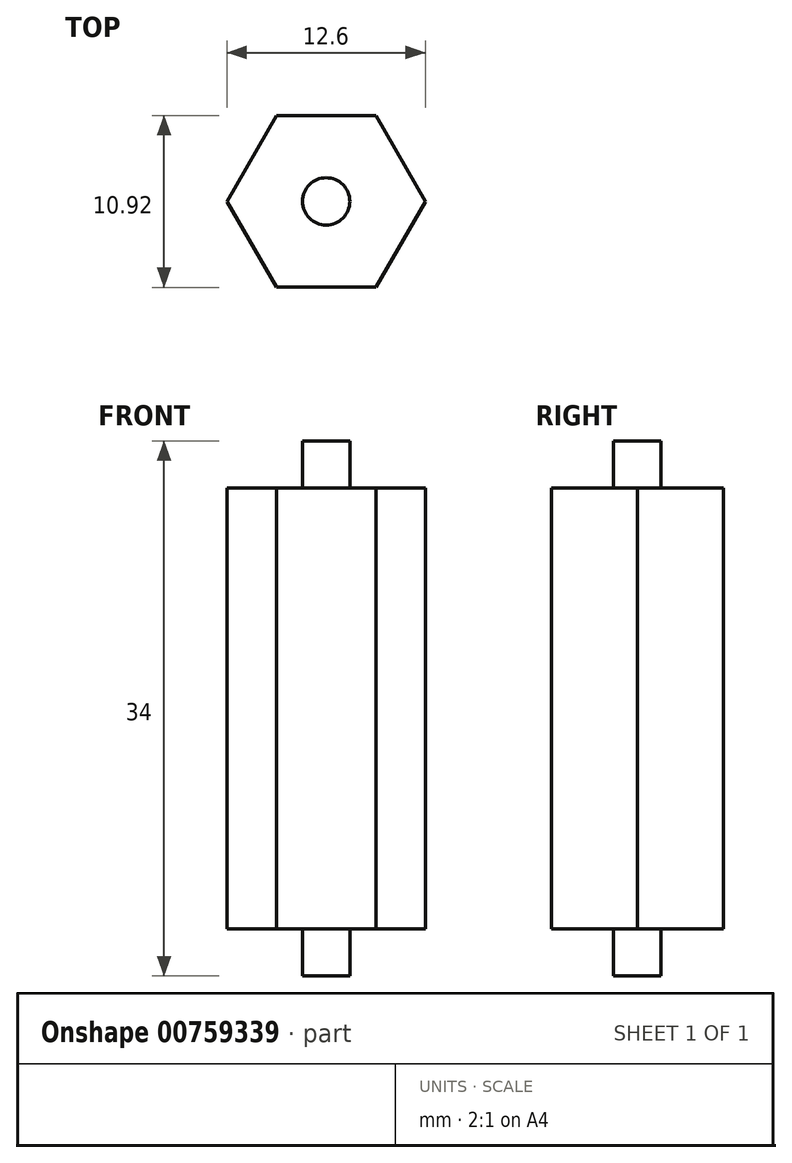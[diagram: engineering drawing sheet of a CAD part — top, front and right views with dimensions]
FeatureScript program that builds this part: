
annotation { "Feature Type Name" : "Feature", "Feature Type Description" : "" }
export const myFeature = defineFeature(function(context is Context, id is Id, definition is map)
    precondition{}
    {
        {
            var Q0;
            Q0=qCreatedBy(makeId("Top.planeOp"),FACE);
            var sketch = newSketch(context, id + "F0", { "sketchPlane" : qUnion([Q0])});
            skCircle(sketch, "E0.cCircle", {"center": v(0, 0) * mm, "radius": 5.46 * mm, "construction": true});
            skLineSegment(sketch, "E0.0", {"start": v(-3.15, 5.46) * mm, "end": v(3.15, 5.46) * mm});
            skLineSegment(sketch, "E0.1", {"start": v(3.15, 5.46) * mm, "end": v(6.3, 0) * mm});
            skLineSegment(sketch, "E0.2", {"start": v(6.3, 0) * mm, "end": v(3.15, -5.46) * mm});
            skLineSegment(sketch, "E0.3", {"start": v(3.15, -5.46) * mm, "end": v(-3.15, -5.46) * mm});
            skLineSegment(sketch, "E0.4", {"start": v(-3.15, -5.46) * mm, "end": v(-6.3, 0) * mm});
            skLineSegment(sketch, "E0.5", {"start": v(-6.3, 0) * mm, "end": v(-3.15, 5.46) * mm});
            skPoint(sketch, "E0.0.midPoint", {"position": v(0, 5.46) * mm});
            skSolve(sketch);
        }
        {
            var Q0;
            Q0=makeQuery(id+"F0.imprint","IMPRINT",FACE,{"disambiguationData":[TD([[makeQuery(id+"F0.imprint","IMPRINT",EDGE,{"derivedFrom":sQuery(id+"F0.wireOp",EDGE,"E0.0")}),-1.0]])]});
            extrude(context, id + "F1", {"entities" : qUnion([Q0]), "depth" : 28 * mm, "offsetDistance" : 25 * mm});
        }
        {
            var Q0;
            Q0=makeQuery(id+"F1.opExtrude","CAP_FACE",FACE,{"disambiguationData":[OSD([sQuery(id+"F0.wireOp",EDGE,"E0.0"),sQuery(id+"F0.wireOp",EDGE,"E0.1"),sQuery(id+"F0.wireOp",EDGE,"E0.2"),sQuery(id+"F0.wireOp",EDGE,"E0.3"),sQuery(id+"F0.wireOp",EDGE,"E0.4"),sQuery(id+"F0.wireOp",EDGE,"E0.5")])],"isStart":false});
            var sketch = newSketch(context, id + "F2", { "sketchPlane" : qUnion([Q0])});
            skCircle(sketch, "E1", {"center": v(0, 0) * mm, "radius": 1.5 * mm});
            skSolve(sketch);
        }
        {
            var Q0;
            Q0=makeQuery(id+"F2.imprint","IMPRINT",FACE,{"disambiguationData":[TD([[makeQuery(id+"F2.imprint","IMPRINT",EDGE,{"derivedFrom":sQuery(id+"F2.wireOp",EDGE,"E1")}),1.0]])]});
            extrude(context, id + "F3", {"entities" : qUnion([Q0]), "depth" : 3 * mm, "offsetDistance" : 25 * mm});
        }
        {
            var Q0;
            Q0=makeQuery(id+"F1.opExtrude","CAP_FACE",FACE,{"disambiguationData":[OSD([sQuery(id+"F0.wireOp",EDGE,"E0.0"),sQuery(id+"F0.wireOp",EDGE,"E0.1"),sQuery(id+"F0.wireOp",EDGE,"E0.2"),sQuery(id+"F0.wireOp",EDGE,"E0.3"),sQuery(id+"F0.wireOp",EDGE,"E0.4"),sQuery(id+"F0.wireOp",EDGE,"E0.5")])],"isStart":true});
            var sketch = newSketch(context, id + "F4", { "sketchPlane" : qUnion([Q0])});
            skCircle(sketch, "E2", {"center": v(0, 0) * mm, "radius": 1.5 * mm});
            skSolve(sketch);
        }
        {
            var Q0;
            Q0=makeQuery(id+"F4.imprint","IMPRINT",FACE,{"disambiguationData":[TD([[makeQuery(id+"F4.imprint","IMPRINT",EDGE,{"derivedFrom":sQuery(id+"F4.wireOp",EDGE,"E2")}),1.0]])]});
            extrude(context, id + "F5", {"entities" : qUnion([Q0]), "operationType" : NewBodyOperationType.ADD, "depth" : 3 * mm, "offsetDistance" : 25 * mm});
        }
    });
